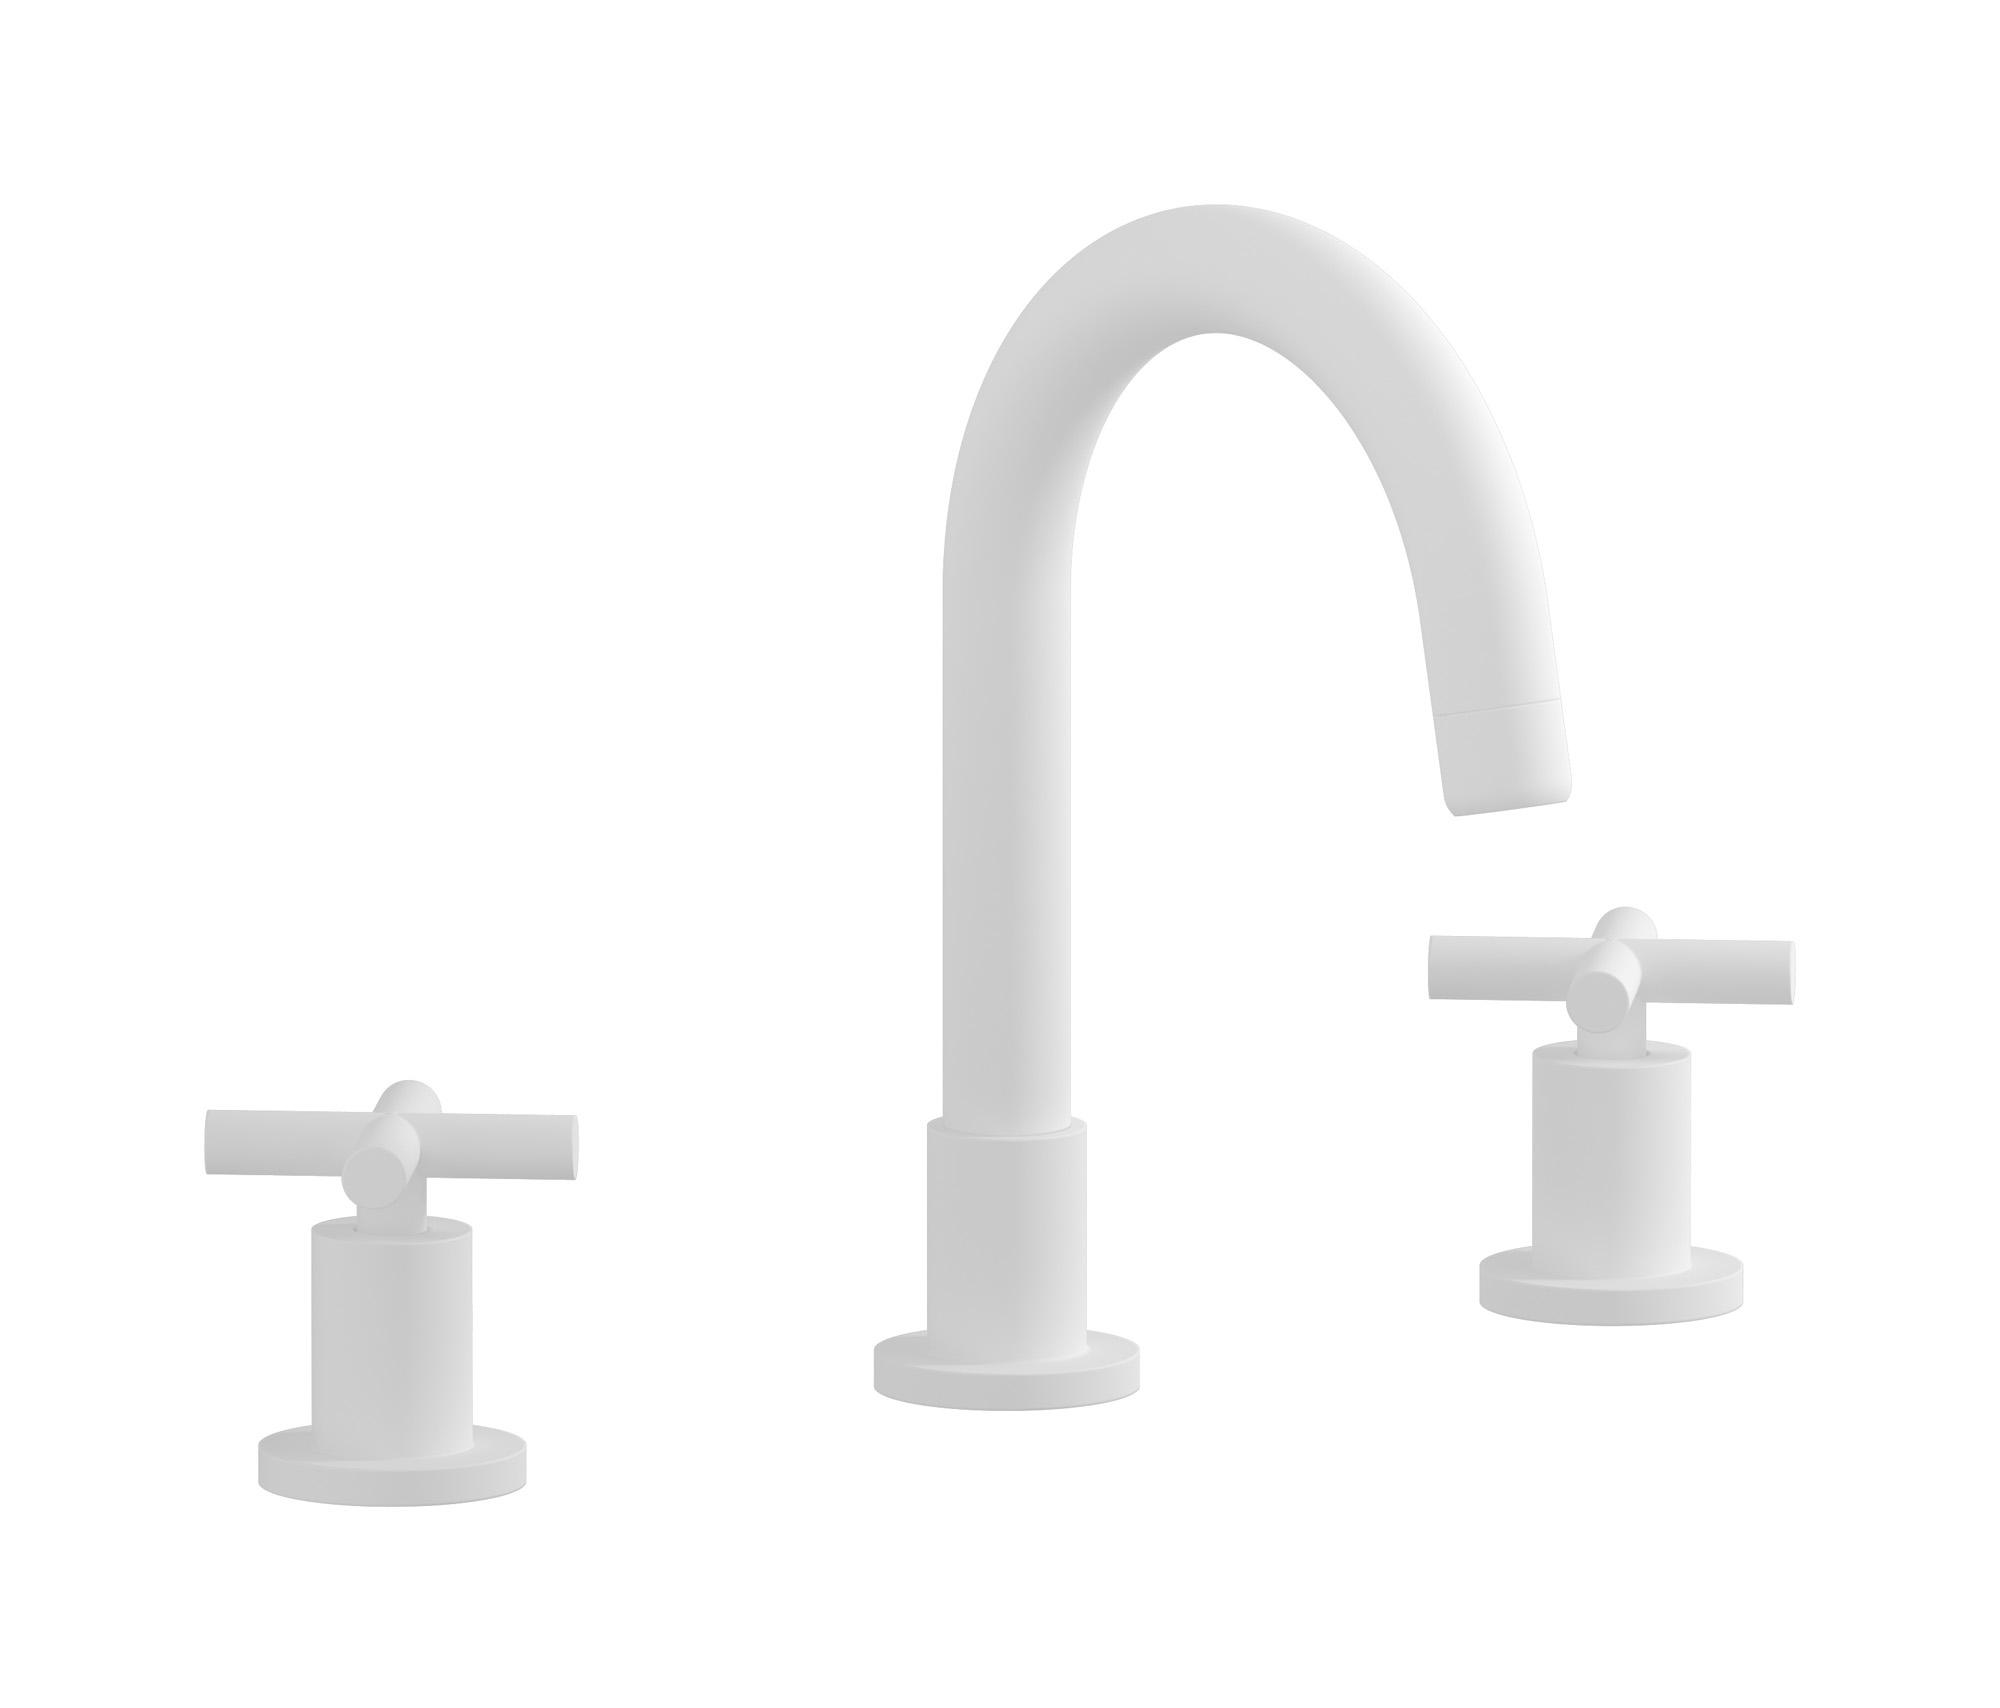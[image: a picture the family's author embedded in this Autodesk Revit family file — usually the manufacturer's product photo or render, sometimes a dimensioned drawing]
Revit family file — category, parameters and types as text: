
# Revit family: WO390
name_source: partatom
category: Apparecchi idraulici
units: mm (PartAtom-declared; Revit-internal decimal feet)

## family parameters
Basato su piano di lavoro = No
Condiviso = No
Mantieni orientamento annotazione = No
Numero OmniClass = 23.45.55.17
Punto di calcolo locali = No
Quota connettore circolare = Usa diametro
Sempre verticale = Sì
Taglio con vuoti quando caricato = No
Tipo di parte = Normale
Titolo OmniClass = Mixing Faucets

## types (5) — shared parameters
Cold water inlet = 10 mm  [stored 0.0328084 ft]
Commenti sul tipo = Washbasin mixer
Connessione CW = No
Connessione HW = No
Connessione di scarico = No
Connessione di ventilazione = No
Descrizione = Three holes washbasin set with tall spout
Hot water inlet = 10 mm  [stored 0.0328084 ft]
Produttore = IB Rubinetterie S.p.A.
URL = https://www.weareib.it
zero-valued in all types: Prospetto di default

## per-type parameters (varying)
| type | Finishes surface | Immagine tipo | Modello |
| Chrome | IB_Chrome | WO390CC.jpg | WO390CC |
| Brushed nickel | IB_Brushed nickel | WO390SS.jpg | WO390SS |
| Matt black | IB_matt black | WO390NP.jpg | WO390NP |
| Matt white | IB_matt white | WO390BO.jpg | WO390BO |
| Gold | IB_gold | WO390OO.jpg | WO390OO |

note: [stored X ft] marks values corroborated as IEEE doubles in the binary element streams (Revit-internal decimal feet)
